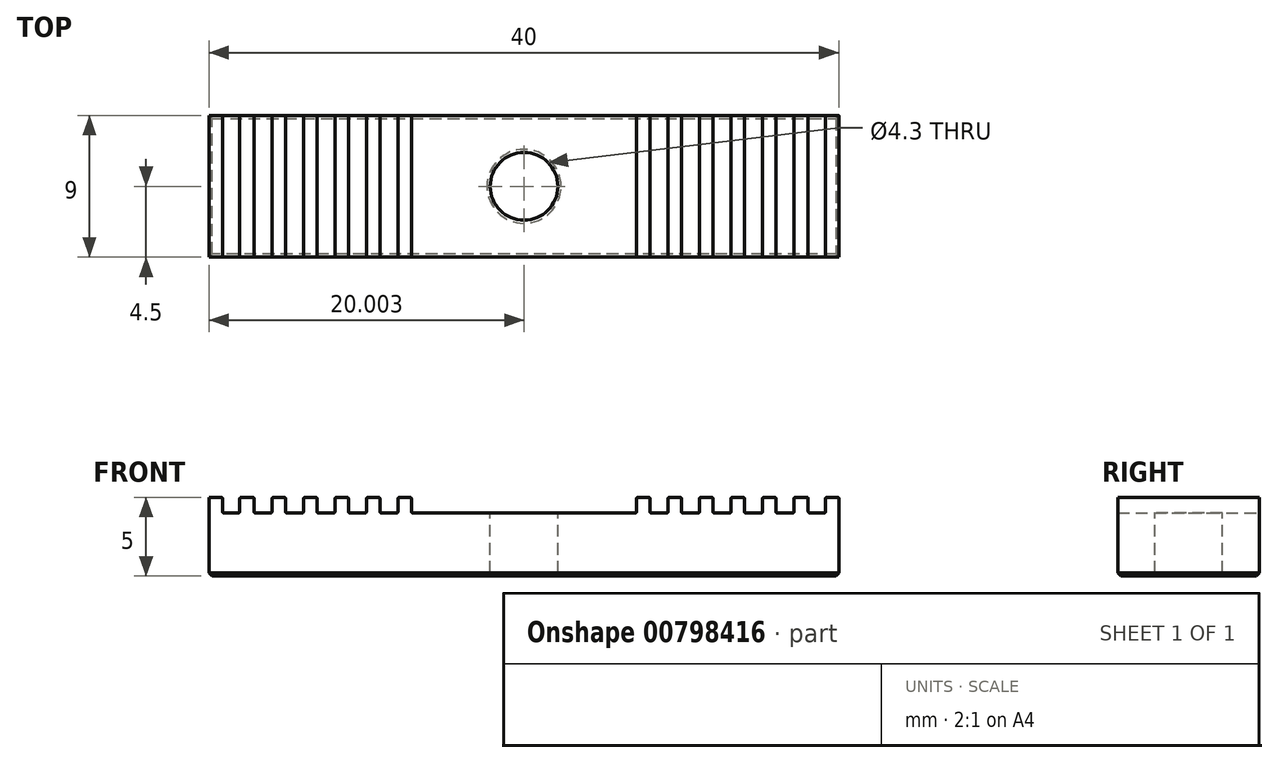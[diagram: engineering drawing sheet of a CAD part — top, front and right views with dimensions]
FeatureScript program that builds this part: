
annotation { "Feature Type Name" : "Feature", "Feature Type Description" : "" }
export const myFeature = defineFeature(function(context is Context, id is Id, definition is map)
    precondition{}
    {
        {
            var Q0;
            Q0=qCreatedBy(makeId("Front.planeOp"),FACE);
            var sketch = newSketch(context, id + "F0", { "sketchPlane" : qUnion([Q0])});
            skLineSegment(sketch, "E0.bottom", {"start": v(-27.06, -1) * mm, "end": v(-26.2, -1) * mm});
            skLineSegment(sketch, "E0.top", {"start": v(-27.06, -6) * mm, "end": v(-7.06, -6) * mm});
            skLineSegment(sketch, "E0.left", {"start": v(-27.06, -1) * mm, "end": v(-27.06, -6) * mm});
            skLineSegment(sketch, "E1", {"start": v(-26.2, -2) * mm, "end": v(-25.1, -2) * mm, "construction": true});
            skPoint(sketch, "E2", {"position": v(-26.2, -2) * mm});
            skPoint(sketch, "E3", {"position": v(-25.1, -2) * mm});
            skLineSegment(sketch, "E4", {"start": v(-26.2, -1) * mm, "end": v(-26.2, -2) * mm});
            skLineSegment(sketch, "E5", {"start": v(-25.1, -2) * mm, "end": v(-25.1, -1) * mm});
            skPoint(sketch, "E6.orphan", {"position": v(-26.2, -6) * mm});
            skPoint(sketch, "E7.orphan", {"position": v(-25.06, -6) * mm});
            skLineSegment(sketch, "E8", {"start": v(-26.2, -2) * mm, "end": v(-25.1, -2) * mm});
            skLineSegment(sketch, "E9", {"start": v(-24.2, -1) * mm, "end": v(-24.2, -2) * mm, "construction": true});
            skLineSegment(sketch, "E10", {"start": v(-25.1, -1) * mm, "end": v(-24.2, -1) * mm});
            skPoint(sketch, "E11.end.orphan", {"position": v(-23.06, -6) * mm});
            skLineSegment(sketch, "E12", {"start": v(-23.06, -2) * mm, "end": v(-23.06, -1) * mm, "construction": true});
            skLineSegment(sketch, "E13", {"start": v(-22.2, -1) * mm, "end": v(-22.2, -2) * mm, "construction": true});
            skLineSegment(sketch, "E14", {"start": v(-21.06, -1) * mm, "end": v(-21.06, -2) * mm, "construction": true});
            skLineSegment(sketch, "E15", {"start": v(-20.2, -1) * mm, "end": v(-20.2, -2) * mm, "construction": true});
            skLineSegment(sketch, "E16", {"start": v(-19.06, -1) * mm, "end": v(-19.06, -2) * mm, "construction": true});
            skPoint(sketch, "E17", {"position": v(-24.2, -2) * mm});
            skPoint(sketch, "E18", {"position": v(-23.06, -2) * mm});
            skPoint(sketch, "E19", {"position": v(-22.2, -2) * mm});
            skPoint(sketch, "E20", {"position": v(-21.06, -2) * mm});
            skPoint(sketch, "E21", {"position": v(-20.2, -2) * mm});
            skPoint(sketch, "E22", {"position": v(-19.06, -2) * mm});
            skLineSegment(sketch, "E23", {"start": v(-24.2, -1) * mm, "end": v(-24.2, -2) * mm});
            skLineSegment(sketch, "E24", {"start": v(-23.06, -2) * mm, "end": v(-23.06, -1) * mm});
            skLineSegment(sketch, "E25", {"start": v(-22.2, -1) * mm, "end": v(-22.2, -2) * mm});
            skLineSegment(sketch, "E26", {"start": v(-21.06, -2) * mm, "end": v(-21.06, -1) * mm});
            skLineSegment(sketch, "E27", {"start": v(-20.2, -1) * mm, "end": v(-20.2, -2) * mm});
            skLineSegment(sketch, "E28", {"start": v(-19.06, -2) * mm, "end": v(-19.06, -1) * mm});
            skPoint(sketch, "E29.orphan", {"position": v(-24.2, -6) * mm});
            skPoint(sketch, "E30.orphan", {"position": v(-22.2, -6) * mm});
            skPoint(sketch, "E31.orphan", {"position": v(-21.06, -6) * mm});
            skPoint(sketch, "E32.orphan", {"position": v(-20.2, -6) * mm});
            skPoint(sketch, "E33.orphan", {"position": v(-19.06, -6) * mm});
            skLineSegment(sketch, "E34.trimOffspring", {"start": v(-24.2, -2) * mm, "end": v(-23.06, -2) * mm, "construction": true});
            skLineSegment(sketch, "E35", {"start": v(-24.2, -2) * mm, "end": v(-23.06, -2) * mm});
            skLineSegment(sketch, "E36", {"start": v(-22.2, -2) * mm, "end": v(-21.06, -2) * mm});
            skLineSegment(sketch, "E37", {"start": v(-20.2, -2) * mm, "end": v(-19.06, -2) * mm});
            skLineSegment(sketch, "E38.trimOffspring", {"start": v(-22.2, -2) * mm, "end": v(-21.06, -2) * mm, "construction": true});
            skLineSegment(sketch, "E39.trimOffspring", {"start": v(-20.2, -2) * mm, "end": v(-19.06, -2) * mm, "construction": true});
            skLineSegment(sketch, "E40", {"start": v(-18.2, -1) * mm, "end": v(-18.2, -2) * mm, "construction": true});
            skLineSegment(sketch, "E41", {"start": v(-17.06, -1) * mm, "end": v(-17.06, -2) * mm, "construction": true});
            skLineSegment(sketch, "E42", {"start": v(-16.2, -1) * mm, "end": v(-16.2, -2) * mm, "construction": true});
            skLineSegment(sketch, "E43", {"start": v(-15.06, -1) * mm, "end": v(-15.06, -2) * mm, "construction": true});
            skLineSegment(sketch, "E44", {"start": v(-14.2, -1) * mm, "end": v(-14.2, -2) * mm, "construction": true});
            skPoint(sketch, "E45", {"position": v(-18.2, -2) * mm});
            skPoint(sketch, "E46", {"position": v(-17.06, -2) * mm});
            skPoint(sketch, "E47", {"position": v(-16.2, -2) * mm});
            skPoint(sketch, "E48", {"position": v(-15.06, -2) * mm});
            skPoint(sketch, "E49", {"position": v(-14.2, -2) * mm});
            skLineSegment(sketch, "E50", {"start": v(-18.2, -1) * mm, "end": v(-18.2, -2) * mm});
            skLineSegment(sketch, "E51", {"start": v(-18.2, -2) * mm, "end": v(-17.06, -2) * mm});
            skLineSegment(sketch, "E52", {"start": v(-17.06, -1) * mm, "end": v(-17.06, -2) * mm});
            skLineSegment(sketch, "E53", {"start": v(-16.2, -1) * mm, "end": v(-16.2, -2) * mm});
            skLineSegment(sketch, "E54", {"start": v(-16.2, -2) * mm, "end": v(-15.06, -2) * mm});
            skLineSegment(sketch, "E55", {"start": v(-15.06, -1) * mm, "end": v(-15.06, -2) * mm});
            skLineSegment(sketch, "E56", {"start": v(-14.2, -1) * mm, "end": v(-14.2, -2) * mm});
            skLineSegment(sketch, "E57.trimOffspring", {"start": v(-18.2, -2) * mm, "end": v(-17.06, -2) * mm, "construction": true});
            skPoint(sketch, "E58.orphan", {"position": v(-18.2, -6) * mm});
            skPoint(sketch, "E59.orphan", {"position": v(-17.06, -6) * mm});
            skLineSegment(sketch, "E60.trimOffspring", {"start": v(-16.2, -2) * mm, "end": v(-15.06, -2) * mm, "construction": true});
            skPoint(sketch, "E61.orphan", {"position": v(-16.2, -6) * mm});
            skPoint(sketch, "E62.orphan", {"position": v(-15.06, -6) * mm});
            skLineSegment(sketch, "E63.trimOffspring", {"start": v(-14.2, -2) * mm, "end": v(-7.06, -2) * mm, "construction": true});
            skPoint(sketch, "E64.orphan", {"position": v(-14.2, -6) * mm});
            skLineSegment(sketch, "E65", {"start": v(-14.2, -2) * mm, "end": v(-7.06, -2) * mm});
            skLineSegment(sketch, "E66.trimOffspring", {"start": v(-15.06, -1) * mm, "end": v(-14.2, -1) * mm});
            skLineSegment(sketch, "E67.trimOffspring", {"start": v(-17.06, -1) * mm, "end": v(-16.2, -1) * mm});
            skLineSegment(sketch, "E68.trimOffspring", {"start": v(-19.06, -1) * mm, "end": v(-18.2, -1) * mm});
            skLineSegment(sketch, "E69.trimOffspring", {"start": v(-21.06, -1) * mm, "end": v(-20.2, -1) * mm});
            skLineSegment(sketch, "E70.trimOffspring", {"start": v(-23.06, -1) * mm, "end": v(-22.2, -1) * mm});
            skLineSegment(sketch, "E71.MirrorCS", {"start": v(8.1, -2) * mm, "end": v(6.94, -2) * mm});
            skLineSegment(sketch, "E72.MirrorCS", {"start": v(6.94, -2) * mm, "end": v(6.94, -1) * mm});
            skLineSegment(sketch, "E73.MirrorCS", {"start": v(12.1, -2) * mm, "end": v(11, -2) * mm});
            skLineSegment(sketch, "E74.MirrorCS", {"start": v(2.94, -1) * mm, "end": v(2.94, -2) * mm});
            skLineSegment(sketch, "E75.MirrorCS", {"start": v(0.1, -2) * mm, "end": v(-7.06, -2) * mm});
            skLineSegment(sketch, "E76.MirrorCS", {"start": v(6.1, -1) * mm, "end": v(6.1, -2) * mm});
            skLineSegment(sketch, "E77.MirrorCS", {"start": v(0.1, -1) * mm, "end": v(0.1, -2) * mm});
            skLineSegment(sketch, "E78.MirrorCS", {"start": v(0.94, -1) * mm, "end": v(0.94, -2) * mm});
            skLineSegment(sketch, "E79.MirrorCS", {"start": v(2.1, -1) * mm, "end": v(2.1, -2) * mm});
            skLineSegment(sketch, "E80.MirrorCS", {"start": v(6.1, -2) * mm, "end": v(4.94, -2) * mm});
            skLineSegment(sketch, "E81.MirrorCS", {"start": v(8.1, -1) * mm, "end": v(8.1, -2) * mm});
            skLineSegment(sketch, "E82.MirrorCS", {"start": v(4.1, -1) * mm, "end": v(4.1, -2) * mm});
            skLineSegment(sketch, "E83.MirrorCS", {"start": v(8.94, -2) * mm, "end": v(8.94, -1) * mm});
            skLineSegment(sketch, "E84.MirrorCS", {"start": v(4.94, -2) * mm, "end": v(4.94, -1) * mm});
            skLineSegment(sketch, "E85.MirrorCS", {"start": v(4.1, -2) * mm, "end": v(2.94, -2) * mm});
            skLineSegment(sketch, "E86.MirrorCS", {"start": v(10.1, -2) * mm, "end": v(8.94, -2) * mm});
            skLineSegment(sketch, "E87.MirrorCS", {"start": v(11, -1) * mm, "end": v(10.1, -1) * mm});
            skLineSegment(sketch, "E88.MirrorCS", {"start": v(2.1, -2) * mm, "end": v(0.94, -2) * mm});
            skLineSegment(sketch, "E89.MirrorCS", {"start": v(10.1, -1) * mm, "end": v(10.1, -2) * mm});
            skLineSegment(sketch, "E90.MirrorCS", {"start": v(2.1, -2) * mm, "end": v(0.94, -2) * mm, "construction": true});
            skLineSegment(sketch, "E91.MirrorCS", {"start": v(4.1, -1) * mm, "end": v(4.1, -2) * mm, "construction": true});
            skLineSegment(sketch, "E92.MirrorCS", {"start": v(4.94, -1) * mm, "end": v(4.1, -1) * mm});
            skLineSegment(sketch, "E93.MirrorCS", {"start": v(12.94, -6) * mm, "end": v(-7.06, -6) * mm});
            skPoint(sketch, "E94.MirrorP", {"position": v(6.1, -6) * mm});
            skLineSegment(sketch, "E95.MirrorCS", {"start": v(8.1, -1) * mm, "end": v(8.1, -2) * mm, "construction": true});
            skPoint(sketch, "E96.MirrorP", {"position": v(6.94, -2) * mm});
            skLineSegment(sketch, "E97.MirrorCS", {"start": v(2.94, -1) * mm, "end": v(2.1, -1) * mm});
            skLineSegment(sketch, "E98.MirrorCS", {"start": v(10.1, -1) * mm, "end": v(10.1, -2) * mm, "construction": true});
            skLineSegment(sketch, "E99.MirrorCS", {"start": v(8.94, -2) * mm, "end": v(8.94, -1) * mm, "construction": true});
            skLineSegment(sketch, "E100.MirrorCS", {"start": v(0.94, -1) * mm, "end": v(0.1, -1) * mm});
            skPoint(sketch, "E101.MirrorP", {"position": v(8.1, -2) * mm});
            skLineSegment(sketch, "E102.MirrorCS", {"start": v(12.1, -1) * mm, "end": v(12.1, -2) * mm});
            skPoint(sketch, "E103.MirrorP", {"position": v(2.1, -6) * mm});
            skPoint(sketch, "E104.MirrorP", {"position": v(8.94, -2) * mm});
            skPoint(sketch, "E105.MirrorP", {"position": v(0.94, -6) * mm});
            skPoint(sketch, "E106.MirrorP", {"position": v(4.1, -6) * mm});
            skPoint(sketch, "E107.MirrorP", {"position": v(4.94, -6) * mm});
            skPoint(sketch, "E108.MirrorP", {"position": v(2.94, -2) * mm});
            skPoint(sketch, "E109.MirrorP", {"position": v(6.94, -6) * mm});
            skLineSegment(sketch, "E110.MirrorCS", {"start": v(11, -2) * mm, "end": v(11, -1) * mm});
            skPoint(sketch, "E111.MirrorP", {"position": v(10.1, -2) * mm});
            skPoint(sketch, "E112.MirrorP", {"position": v(4.1, -2) * mm});
            skLineSegment(sketch, "E113.MirrorCS", {"start": v(6.1, -1) * mm, "end": v(6.1, -2) * mm, "construction": true});
            skLineSegment(sketch, "E114.MirrorCS", {"start": v(12.94, -1) * mm, "end": v(12.1, -1) * mm});
            skPoint(sketch, "E115.MirrorP", {"position": v(0.94, -2) * mm});
            skLineSegment(sketch, "E116.MirrorCS", {"start": v(2.1, -1) * mm, "end": v(2.1, -2) * mm, "construction": true});
            skLineSegment(sketch, "E117.MirrorCS", {"start": v(6.94, -1) * mm, "end": v(6.1, -1) * mm});
            skLineSegment(sketch, "E118.MirrorCS", {"start": v(2.94, -1) * mm, "end": v(2.94, -2) * mm, "construction": true});
            skLineSegment(sketch, "E119.MirrorCS", {"start": v(0.1, -2) * mm, "end": v(-7.06, -2) * mm, "construction": true});
            skLineSegment(sketch, "E120.MirrorCS", {"start": v(4.94, -1) * mm, "end": v(4.94, -2) * mm, "construction": true});
            skLineSegment(sketch, "E121.MirrorCS", {"start": v(0.1, -1) * mm, "end": v(0.1, -2) * mm, "construction": true});
            skLineSegment(sketch, "E122.MirrorCS", {"start": v(6.1, -2) * mm, "end": v(4.94, -2) * mm, "construction": true});
            skLineSegment(sketch, "E123.MirrorCS", {"start": v(0.94, -1) * mm, "end": v(0.94, -2) * mm, "construction": true});
            skLineSegment(sketch, "E124.MirrorCS", {"start": v(4.1, -2) * mm, "end": v(2.94, -2) * mm, "construction": true});
            skPoint(sketch, "E125.MirrorP", {"position": v(11, -2) * mm});
            skLineSegment(sketch, "E126.MirrorCS", {"start": v(6.94, -1) * mm, "end": v(6.94, -2) * mm, "construction": true});
            skLineSegment(sketch, "E127.MirrorCS", {"start": v(12.1, -2) * mm, "end": v(11, -2) * mm, "construction": true});
            skPoint(sketch, "E128.MirrorP", {"position": v(4.94, -2) * mm});
            skLineSegment(sketch, "E129.MirrorCS", {"start": v(12.94, -1) * mm, "end": v(12.94, -6) * mm});
            skPoint(sketch, "E130.MirrorP", {"position": v(8.94, -6) * mm});
            skLineSegment(sketch, "E131.MirrorCS", {"start": v(8.1, -2) * mm, "end": v(6.94, -2) * mm, "construction": true});
            skPoint(sketch, "E132.MirrorP", {"position": v(12.1, -6) * mm});
            skPoint(sketch, "E133.MirrorP", {"position": v(0.1, -6) * mm});
            skPoint(sketch, "E134.MirrorP", {"position": v(10.1, -6) * mm});
            skPoint(sketch, "E135.MirrorP", {"position": v(2.94, -6) * mm});
            skLineSegment(sketch, "E136.MirrorCS", {"start": v(8.94, -1) * mm, "end": v(8.1, -1) * mm});
            skPoint(sketch, "E137.MirrorP", {"position": v(6.1, -2) * mm});
            skPoint(sketch, "E138.MirrorP", {"position": v(2.1, -2) * mm});
            skLineSegment(sketch, "E139.MirrorCS", {"start": v(10.1, -2) * mm, "end": v(8.94, -2) * mm, "construction": true});
            skPoint(sketch, "E140.MirrorP", {"position": v(0.1, -2) * mm});
            skPoint(sketch, "E141.MirrorP", {"position": v(10.94, -6) * mm});
            skPoint(sketch, "E142.MirrorP", {"position": v(12.1, -2) * mm});
            skPoint(sketch, "E143.MirrorP", {"position": v(8.1, -6) * mm});
            skSolve(sketch);
        }
        {
            var Q0;
            Q0=makeQuery(id+"F0.imprint","IMPRINT",FACE,{"disambiguationData":[TD([[makeQuery(id+"F0.imprint","IMPRINT",EDGE,{"derivedFrom":sQuery(id+"F0.wireOp",EDGE,"E0.bottom")}),-1.0]])]});
            extrude(context, id + "F1", {"entities" : qUnion([Q0]), "depth" : 9 * mm, "offsetDistance" : 25 * mm});
        }
        {
            var Q0;
            Q0=makeQuery(id+"F1.opExtrude","SWEPT_FACE",FACE,{"disambiguationData":[OSD([sQuery(id+"F0.wireOp",EDGE,"E65"),sQuery(id+"F0.wireOp",EDGE,"E75.MirrorCS")])]});
            var sketch = newSketch(context, id + "F2", { "sketchPlane" : qUnion([Q0])});
            skLineSegment(sketch, "E144", {"start": v(-7.06, 0) * mm, "end": v(-7.06, -9) * mm, "construction": true});
            skPoint(sketch, "E145", {"position": v(-7.06, -4.5) * mm});
            skSolve(sketch);
        }
        {
            var Q0;
            Q0=sQuery(id+"F2.wireOp",VERTEX,"E145");
            var Q1;
            Q1=makeQuery(id+"F1.opExtrude","SWEPT_BODY",BODY,{"disambiguationData":[OSD([sQuery(id+"F0.wireOp",EDGE,"E0.bottom"),sQuery(id+"F0.wireOp",EDGE,"E0.top"),sQuery(id+"F0.wireOp",EDGE,"E0.left"),sQuery(id+"F0.wireOp",EDGE,"E4"),sQuery(id+"F0.wireOp",EDGE,"E5"),sQuery(id+"F0.wireOp",EDGE,"E8"),sQuery(id+"F0.wireOp",EDGE,"E23"),sQuery(id+"F0.wireOp",EDGE,"E24"),sQuery(id+"F0.wireOp",EDGE,"E25"),sQuery(id+"F0.wireOp",EDGE,"E26"),sQuery(id+"F0.wireOp",EDGE,"E27"),sQuery(id+"F0.wireOp",EDGE,"E28"),sQuery(id+"F0.wireOp",EDGE,"E35"),sQuery(id+"F0.wireOp",EDGE,"E36"),sQuery(id+"F0.wireOp",EDGE,"E37"),sQuery(id+"F0.wireOp",EDGE,"E50"),sQuery(id+"F0.wireOp",EDGE,"E51"),sQuery(id+"F0.wireOp",EDGE,"E52"),sQuery(id+"F0.wireOp",EDGE,"E53"),sQuery(id+"F0.wireOp",EDGE,"E54"),sQuery(id+"F0.wireOp",EDGE,"E55"),sQuery(id+"F0.wireOp",EDGE,"E56"),sQuery(id+"F0.wireOp",EDGE,"E65"),sQuery(id+"F0.wireOp",EDGE,"E66.trimOffspring"),sQuery(id+"F0.wireOp",EDGE,"E67.trimOffspring"),sQuery(id+"F0.wireOp",EDGE,"E68.trimOffspring"),sQuery(id+"F0.wireOp",EDGE,"E69.trimOffspring"),sQuery(id+"F0.wireOp",EDGE,"E70.trimOffspring"),sQuery(id+"F0.wireOp",EDGE,"E10"),sQuery(id+"F0.wireOp",EDGE,"E71.MirrorCS"),sQuery(id+"F0.wireOp",EDGE,"E72.MirrorCS"),sQuery(id+"F0.wireOp",EDGE,"E73.MirrorCS"),sQuery(id+"F0.wireOp",EDGE,"E74.MirrorCS"),sQuery(id+"F0.wireOp",EDGE,"E75.MirrorCS"),sQuery(id+"F0.wireOp",EDGE,"E76.MirrorCS"),sQuery(id+"F0.wireOp",EDGE,"E77.MirrorCS"),sQuery(id+"F0.wireOp",EDGE,"E78.MirrorCS"),sQuery(id+"F0.wireOp",EDGE,"E79.MirrorCS"),sQuery(id+"F0.wireOp",EDGE,"E80.MirrorCS"),sQuery(id+"F0.wireOp",EDGE,"E81.MirrorCS"),sQuery(id+"F0.wireOp",EDGE,"E82.MirrorCS"),sQuery(id+"F0.wireOp",EDGE,"E83.MirrorCS"),sQuery(id+"F0.wireOp",EDGE,"E84.MirrorCS"),sQuery(id+"F0.wireOp",EDGE,"E85.MirrorCS"),sQuery(id+"F0.wireOp",EDGE,"E86.MirrorCS"),sQuery(id+"F0.wireOp",EDGE,"E88.MirrorCS"),sQuery(id+"F0.wireOp",EDGE,"E89.MirrorCS"),sQuery(id+"F0.wireOp",EDGE,"E92.MirrorCS"),sQuery(id+"F0.wireOp",EDGE,"E93.MirrorCS"),sQuery(id+"F0.wireOp",EDGE,"E97.MirrorCS"),sQuery(id+"F0.wireOp",EDGE,"E100.MirrorCS"),sQuery(id+"F0.wireOp",EDGE,"E102.MirrorCS"),sQuery(id+"F0.wireOp",EDGE,"E110.MirrorCS"),sQuery(id+"F0.wireOp",EDGE,"E87.MirrorCS"),sQuery(id+"F0.wireOp",EDGE,"E114.MirrorCS"),sQuery(id+"F0.wireOp",EDGE,"E117.MirrorCS"),sQuery(id+"F0.wireOp",EDGE,"E129.MirrorCS"),sQuery(id+"F0.wireOp",EDGE,"E136.MirrorCS")])]});
            hole(context, id + "F3", {"style" : HoleStyle.SIMPLE, "endStyle" : HoleEndStyle.THROUGH, "standardTappedOrClearance" : lookupTablePath({ "fit" : "Close", "standard" : "ISO", "size" : "M4", "type" : "Clearance" }), "standardBlindInLast" : lookupTablePath({ "fit" : "Close", "standard" : "ISO", "engagement" : "75%", "pitch" : "0.7 mm", "size" : "M4", "type" : "Clearance & tapped" }), "holeDiameter" : 4.3 * mm, "majorDiameter" : 4 * mm, "isTappedThrough" : true, "tappedDepth" : 12 * mm, "tapClearance" : 3, "locations" : qUnion([Q0]), "scope" : qUnion([Q1])});
        }
        {
            var Q0;
            Q0=makeQuery(id+"F1.opExtrude","SWEPT_EDGE",EDGE,{"disambiguationData":[OSD([sQuery(id+"F0.wireOp",EDGE,"E0.bottom"),sQuery(id+"F0.wireOp",EDGE,"E4")])]});
            var Q1;
            Q1=makeQuery(id+"F1.opExtrude","SWEPT_EDGE",EDGE,{"disambiguationData":[OSD([sQuery(id+"F0.wireOp",EDGE,"E4"),sQuery(id+"F0.wireOp",EDGE,"E8")])]});
            var Q2;
            Q2=makeQuery(id+"F1.opExtrude","SWEPT_EDGE",EDGE,{"disambiguationData":[OSD([sQuery(id+"F0.wireOp",EDGE,"E5"),sQuery(id+"F0.wireOp",EDGE,"E10")])]});
            var Q3;
            Q3=makeQuery(id+"F1.opExtrude","SWEPT_EDGE",EDGE,{"disambiguationData":[OSD([sQuery(id+"F0.wireOp",EDGE,"E23"),sQuery(id+"F0.wireOp",EDGE,"E10")])]});
            var Q4;
            Q4=makeQuery(id+"F1.opExtrude","SWEPT_EDGE",EDGE,{"disambiguationData":[OSD([sQuery(id+"F0.wireOp",EDGE,"E23"),sQuery(id+"F0.wireOp",EDGE,"E35")])]});
            var Q5;
            Q5=makeQuery(id+"F1.opExtrude","SWEPT_EDGE",EDGE,{"disambiguationData":[OSD([sQuery(id+"F0.wireOp",EDGE,"E24"),sQuery(id+"F0.wireOp",EDGE,"E70.trimOffspring")])]});
            var Q6;
            Q6=makeQuery(id+"F1.opExtrude","SWEPT_EDGE",EDGE,{"disambiguationData":[OSD([sQuery(id+"F0.wireOp",EDGE,"E25"),sQuery(id+"F0.wireOp",EDGE,"E70.trimOffspring")])]});
            var Q7;
            Q7=makeQuery(id+"F1.opExtrude","SWEPT_EDGE",EDGE,{"disambiguationData":[OSD([sQuery(id+"F0.wireOp",EDGE,"E25"),sQuery(id+"F0.wireOp",EDGE,"E36")])]});
            var Q8;
            Q8=makeQuery(id+"F1.opExtrude","SWEPT_EDGE",EDGE,{"disambiguationData":[OSD([sQuery(id+"F0.wireOp",EDGE,"E26"),sQuery(id+"F0.wireOp",EDGE,"E69.trimOffspring")])]});
            var Q9;
            Q9=makeQuery(id+"F1.opExtrude","SWEPT_EDGE",EDGE,{"disambiguationData":[OSD([sQuery(id+"F0.wireOp",EDGE,"E27"),sQuery(id+"F0.wireOp",EDGE,"E69.trimOffspring")])]});
            var Q10;
            Q10=makeQuery(id+"F1.opExtrude","SWEPT_EDGE",EDGE,{"disambiguationData":[OSD([sQuery(id+"F0.wireOp",EDGE,"E28"),sQuery(id+"F0.wireOp",EDGE,"E68.trimOffspring")])]});
            var Q11;
            Q11=makeQuery(id+"F1.opExtrude","SWEPT_EDGE",EDGE,{"disambiguationData":[OSD([sQuery(id+"F0.wireOp",EDGE,"E50"),sQuery(id+"F0.wireOp",EDGE,"E68.trimOffspring")])]});
            var Q12;
            Q12=makeQuery(id+"F1.opExtrude","SWEPT_EDGE",EDGE,{"disambiguationData":[OSD([sQuery(id+"F0.wireOp",EDGE,"E50"),sQuery(id+"F0.wireOp",EDGE,"E51")])]});
            var Q13;
            Q13=makeQuery(id+"F1.opExtrude","SWEPT_EDGE",EDGE,{"disambiguationData":[OSD([sQuery(id+"F0.wireOp",EDGE,"E27"),sQuery(id+"F0.wireOp",EDGE,"E37")])]});
            var Q14;
            Q14=makeQuery(id+"F1.opExtrude","SWEPT_EDGE",EDGE,{"disambiguationData":[OSD([sQuery(id+"F0.wireOp",EDGE,"E52"),sQuery(id+"F0.wireOp",EDGE,"E67.trimOffspring")])]});
            var Q15;
            Q15=makeQuery(id+"F1.opExtrude","SWEPT_EDGE",EDGE,{"disambiguationData":[OSD([sQuery(id+"F0.wireOp",EDGE,"E53"),sQuery(id+"F0.wireOp",EDGE,"E67.trimOffspring")])]});
            var Q16;
            Q16=makeQuery(id+"F1.opExtrude","SWEPT_EDGE",EDGE,{"disambiguationData":[OSD([sQuery(id+"F0.wireOp",EDGE,"E53"),sQuery(id+"F0.wireOp",EDGE,"E54")])]});
            var Q17;
            Q17=makeQuery(id+"F1.opExtrude","SWEPT_EDGE",EDGE,{"disambiguationData":[OSD([sQuery(id+"F0.wireOp",EDGE,"E55"),sQuery(id+"F0.wireOp",EDGE,"E66.trimOffspring")])]});
            var Q18;
            Q18=makeQuery(id+"F1.opExtrude","SWEPT_EDGE",EDGE,{"disambiguationData":[OSD([sQuery(id+"F0.wireOp",EDGE,"E56"),sQuery(id+"F0.wireOp",EDGE,"E66.trimOffspring")])]});
            var Q19;
            Q19=makeQuery(id+"F1.opExtrude","SWEPT_EDGE",EDGE,{"disambiguationData":[OSD([sQuery(id+"F0.wireOp",EDGE,"E56"),sQuery(id+"F0.wireOp",EDGE,"E65")])]});
            var Q20;
            Q20=makeQuery(id+"F1.opExtrude","SWEPT_EDGE",EDGE,{"disambiguationData":[OSD([sQuery(id+"F0.wireOp",EDGE,"E5"),sQuery(id+"F0.wireOp",EDGE,"E8")])]});
            var Q21;
            Q21=makeQuery(id+"F1.opExtrude","SWEPT_EDGE",EDGE,{"disambiguationData":[OSD([sQuery(id+"F0.wireOp",EDGE,"E24"),sQuery(id+"F0.wireOp",EDGE,"E35")])]});
            var Q22;
            Q22=makeQuery(id+"F1.opExtrude","SWEPT_EDGE",EDGE,{"disambiguationData":[OSD([sQuery(id+"F0.wireOp",EDGE,"E26"),sQuery(id+"F0.wireOp",EDGE,"E36")])]});
            var Q23;
            Q23=makeQuery(id+"F1.opExtrude","SWEPT_EDGE",EDGE,{"disambiguationData":[OSD([sQuery(id+"F0.wireOp",EDGE,"E28"),sQuery(id+"F0.wireOp",EDGE,"E37")])]});
            var Q24;
            Q24=makeQuery(id+"F1.opExtrude","SWEPT_EDGE",EDGE,{"disambiguationData":[OSD([sQuery(id+"F0.wireOp",EDGE,"E51"),sQuery(id+"F0.wireOp",EDGE,"E52")])]});
            var Q25;
            Q25=makeQuery(id+"F1.opExtrude","SWEPT_EDGE",EDGE,{"disambiguationData":[OSD([sQuery(id+"F0.wireOp",EDGE,"E54"),sQuery(id+"F0.wireOp",EDGE,"E55")])]});
            var Q26;
            Q26=makeQuery(id+"F1.opExtrude","SWEPT_EDGE",EDGE,{"disambiguationData":[OSD([sQuery(id+"F0.wireOp",EDGE,"E77.MirrorCS"),sQuery(id+"F0.wireOp",EDGE,"E100.MirrorCS")])]});
            var Q27;
            Q27=makeQuery(id+"F1.opExtrude","SWEPT_EDGE",EDGE,{"disambiguationData":[OSD([sQuery(id+"F0.wireOp",EDGE,"E78.MirrorCS"),sQuery(id+"F0.wireOp",EDGE,"E100.MirrorCS")])]});
            var Q28;
            Q28=makeQuery(id+"F1.opExtrude","SWEPT_EDGE",EDGE,{"disambiguationData":[OSD([sQuery(id+"F0.wireOp",EDGE,"E79.MirrorCS"),sQuery(id+"F0.wireOp",EDGE,"E97.MirrorCS")])]});
            var Q29;
            Q29=makeQuery(id+"F1.opExtrude","SWEPT_EDGE",EDGE,{"disambiguationData":[OSD([sQuery(id+"F0.wireOp",EDGE,"E74.MirrorCS"),sQuery(id+"F0.wireOp",EDGE,"E97.MirrorCS")])]});
            var Q30;
            Q30=makeQuery(id+"F1.opExtrude","SWEPT_EDGE",EDGE,{"disambiguationData":[OSD([sQuery(id+"F0.wireOp",EDGE,"E82.MirrorCS"),sQuery(id+"F0.wireOp",EDGE,"E92.MirrorCS")])]});
            var Q31;
            Q31=makeQuery(id+"F1.opExtrude","SWEPT_EDGE",EDGE,{"disambiguationData":[OSD([sQuery(id+"F0.wireOp",EDGE,"E84.MirrorCS"),sQuery(id+"F0.wireOp",EDGE,"E92.MirrorCS")])]});
            var Q32;
            Q32=makeQuery(id+"F1.opExtrude","SWEPT_EDGE",EDGE,{"disambiguationData":[OSD([sQuery(id+"F0.wireOp",EDGE,"E76.MirrorCS"),sQuery(id+"F0.wireOp",EDGE,"E117.MirrorCS")])]});
            var Q33;
            Q33=makeQuery(id+"F1.opExtrude","SWEPT_EDGE",EDGE,{"disambiguationData":[OSD([sQuery(id+"F0.wireOp",EDGE,"E72.MirrorCS"),sQuery(id+"F0.wireOp",EDGE,"E117.MirrorCS")])]});
            var Q34;
            Q34=makeQuery(id+"F1.opExtrude","SWEPT_EDGE",EDGE,{"disambiguationData":[OSD([sQuery(id+"F0.wireOp",EDGE,"E81.MirrorCS"),sQuery(id+"F0.wireOp",EDGE,"E136.MirrorCS")])]});
            var Q35;
            Q35=makeQuery(id+"F1.opExtrude","SWEPT_EDGE",EDGE,{"disambiguationData":[OSD([sQuery(id+"F0.wireOp",EDGE,"E83.MirrorCS"),sQuery(id+"F0.wireOp",EDGE,"E136.MirrorCS")])]});
            var Q36;
            Q36=makeQuery(id+"F1.opExtrude","SWEPT_EDGE",EDGE,{"disambiguationData":[OSD([sQuery(id+"F0.wireOp",EDGE,"E89.MirrorCS"),sQuery(id+"F0.wireOp",EDGE,"E87.MirrorCS")])]});
            var Q37;
            Q37=makeQuery(id+"F1.opExtrude","SWEPT_EDGE",EDGE,{"disambiguationData":[OSD([sQuery(id+"F0.wireOp",EDGE,"E110.MirrorCS"),sQuery(id+"F0.wireOp",EDGE,"E87.MirrorCS")])]});
            var Q38;
            Q38=makeQuery(id+"F1.opExtrude","SWEPT_EDGE",EDGE,{"disambiguationData":[OSD([sQuery(id+"F0.wireOp",EDGE,"E102.MirrorCS"),sQuery(id+"F0.wireOp",EDGE,"E114.MirrorCS")])]});
            var Q39;
            Q39=makeQuery(id+"F1.opExtrude","SWEPT_EDGE",EDGE,{"disambiguationData":[OSD([sQuery(id+"F0.wireOp",EDGE,"E114.MirrorCS"),sQuery(id+"F0.wireOp",EDGE,"E129.MirrorCS")])]});
            var Q40;
            Q40=makeQuery(id+"F1.opExtrude","SWEPT_EDGE",EDGE,{"disambiguationData":[OSD([sQuery(id+"F0.wireOp",EDGE,"E73.MirrorCS"),sQuery(id+"F0.wireOp",EDGE,"E110.MirrorCS")])]});
            var Q41;
            Q41=makeQuery(id+"F1.opExtrude","SWEPT_EDGE",EDGE,{"disambiguationData":[OSD([sQuery(id+"F0.wireOp",EDGE,"E83.MirrorCS"),sQuery(id+"F0.wireOp",EDGE,"E86.MirrorCS")])]});
            var Q42;
            Q42=makeQuery(id+"F1.opExtrude","SWEPT_EDGE",EDGE,{"disambiguationData":[OSD([sQuery(id+"F0.wireOp",EDGE,"E71.MirrorCS"),sQuery(id+"F0.wireOp",EDGE,"E72.MirrorCS")])]});
            var Q43;
            Q43=makeQuery(id+"F1.opExtrude","SWEPT_EDGE",EDGE,{"disambiguationData":[OSD([sQuery(id+"F0.wireOp",EDGE,"E80.MirrorCS"),sQuery(id+"F0.wireOp",EDGE,"E84.MirrorCS")])]});
            var Q44;
            Q44=makeQuery(id+"F1.opExtrude","SWEPT_EDGE",EDGE,{"disambiguationData":[OSD([sQuery(id+"F0.wireOp",EDGE,"E74.MirrorCS"),sQuery(id+"F0.wireOp",EDGE,"E85.MirrorCS")])]});
            var Q45;
            Q45=makeQuery(id+"F1.opExtrude","SWEPT_EDGE",EDGE,{"disambiguationData":[OSD([sQuery(id+"F0.wireOp",EDGE,"E78.MirrorCS"),sQuery(id+"F0.wireOp",EDGE,"E88.MirrorCS")])]});
            var Q46;
            Q46=makeQuery(id+"F1.opExtrude","SWEPT_EDGE",EDGE,{"disambiguationData":[OSD([sQuery(id+"F0.wireOp",EDGE,"E73.MirrorCS"),sQuery(id+"F0.wireOp",EDGE,"E102.MirrorCS")])]});
            var Q47;
            Q47=makeQuery(id+"F1.opExtrude","SWEPT_EDGE",EDGE,{"disambiguationData":[OSD([sQuery(id+"F0.wireOp",EDGE,"E86.MirrorCS"),sQuery(id+"F0.wireOp",EDGE,"E89.MirrorCS")])]});
            var Q48;
            Q48=makeQuery(id+"F1.opExtrude","SWEPT_EDGE",EDGE,{"disambiguationData":[OSD([sQuery(id+"F0.wireOp",EDGE,"E71.MirrorCS"),sQuery(id+"F0.wireOp",EDGE,"E81.MirrorCS")])]});
            var Q49;
            Q49=makeQuery(id+"F1.opExtrude","SWEPT_EDGE",EDGE,{"disambiguationData":[OSD([sQuery(id+"F0.wireOp",EDGE,"E76.MirrorCS"),sQuery(id+"F0.wireOp",EDGE,"E80.MirrorCS")])]});
            var Q50;
            Q50=makeQuery(id+"F1.opExtrude","SWEPT_EDGE",EDGE,{"disambiguationData":[OSD([sQuery(id+"F0.wireOp",EDGE,"E82.MirrorCS"),sQuery(id+"F0.wireOp",EDGE,"E85.MirrorCS")])]});
            var Q51;
            Q51=makeQuery(id+"F1.opExtrude","SWEPT_EDGE",EDGE,{"disambiguationData":[OSD([sQuery(id+"F0.wireOp",EDGE,"E79.MirrorCS"),sQuery(id+"F0.wireOp",EDGE,"E88.MirrorCS")])]});
            var Q52;
            Q52=makeQuery(id+"F1.opExtrude","SWEPT_EDGE",EDGE,{"disambiguationData":[OSD([sQuery(id+"F0.wireOp",EDGE,"E75.MirrorCS"),sQuery(id+"F0.wireOp",EDGE,"E77.MirrorCS")])]});
            fillet(context, id + "F4", {"entities" : qUnion([Q0, Q1, Q2, Q3, Q4, Q5, Q6, Q7, Q8, Q9, Q10, Q11, Q12, Q13, Q14, Q15, Q16, Q17, Q18, Q19, Q20, Q21, Q22, Q23, Q24, Q25, Q26, Q27, Q28, Q29, Q30, Q31, Q32, Q33, Q34, Q35, Q36, Q37, Q38, Q39, Q40, Q41, Q42, Q43, Q44, Q45, Q46, Q47, Q48, Q49, Q50, Q51, Q52]), "radius" : 0.1 * mm, "tangentPropagation" : true, "allowEdgeOverflow" : false});
        }
        {
            var Q0;
            Q0=makeQuery(id+"F1.opExtrude","SWEPT_FACE",FACE,{"disambiguationData":[OSD([sQuery(id+"F0.wireOp",EDGE,"E0.top"),sQuery(id+"F0.wireOp",EDGE,"E93.MirrorCS")])]});
            var Q1;
            Q1=makeQuery(id+"F3.hole-0.boolean.opBoolean","COPY",EDGE,{"derivedFrom":makeQuery(id+"F3.hole-0.opRevolve","SWEPT_EDGE",EDGE,{"disambiguationData":[OSD([sQuery(id+"F3.hole-0.sketch.wireOp",EDGE,"core_line_2"),sQuery(id+"F3.hole-0.sketch.wireOp",EDGE,"core_line_3")])]})});
            chamfer(context, id + "F5", {"entities" : qUnion([Q0, Q1]), "width" : 0.2 * mm, "tangentPropagation" : true});
        }
    });
